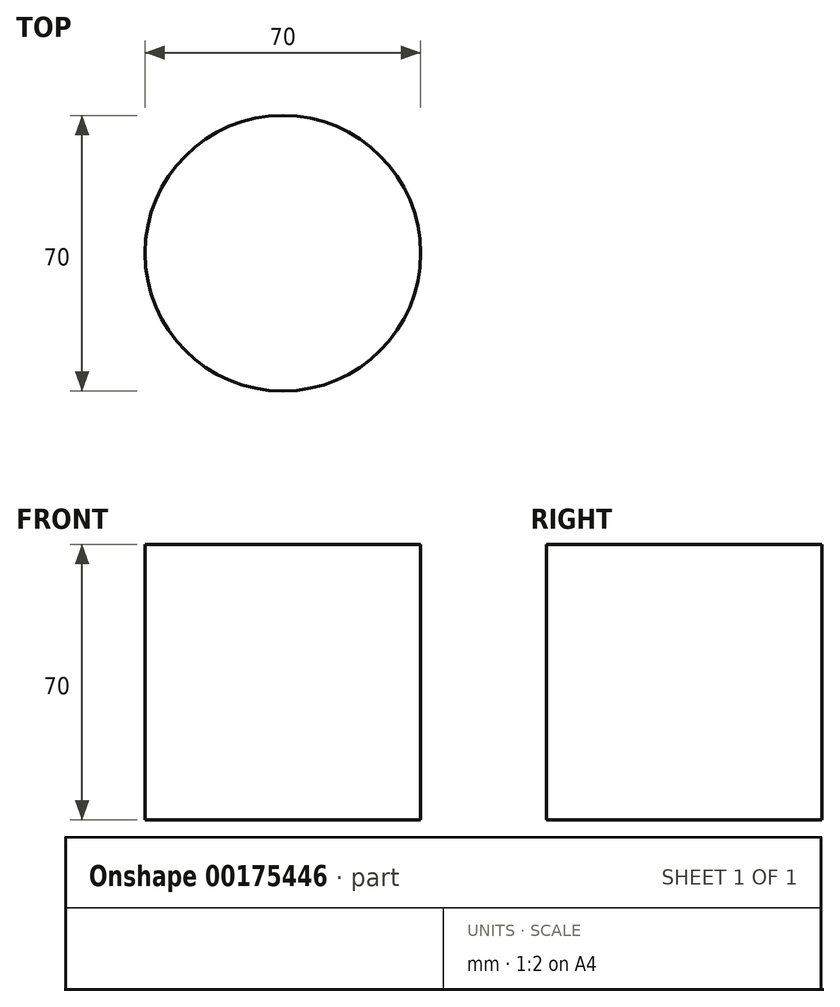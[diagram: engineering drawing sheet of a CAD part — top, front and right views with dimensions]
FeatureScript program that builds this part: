
annotation { "Feature Type Name" : "Feature", "Feature Type Description" : "" }
export const myFeature = defineFeature(function(context is Context, id is Id, definition is map)
    precondition{}
    {
        {
            var Q0;
            Q0=qCreatedBy(makeId("Top.planeOp"),FACE);
            var sketch = newSketch(context, id + "F0", { "sketchPlane" : qUnion([Q0])});
            skCircle(sketch, "E0", {"center": v(0, 0) * mm, "radius": 35 * mm});
            skSolve(sketch);
        }
        {
            var Q0;
            Q0=makeQuery(id+"F0.imprint","IMPRINT",FACE,{"disambiguationData":[TD([[makeQuery(id+"F0.imprint","IMPRINT",EDGE,{"derivedFrom":sQuery(id+"F0.wireOp",EDGE,"E0")}),1.0]])]});
            extrude(context, id + "F1", {"entities" : qUnion([Q0]), "depth" : 70 * mm});
        }
    });
